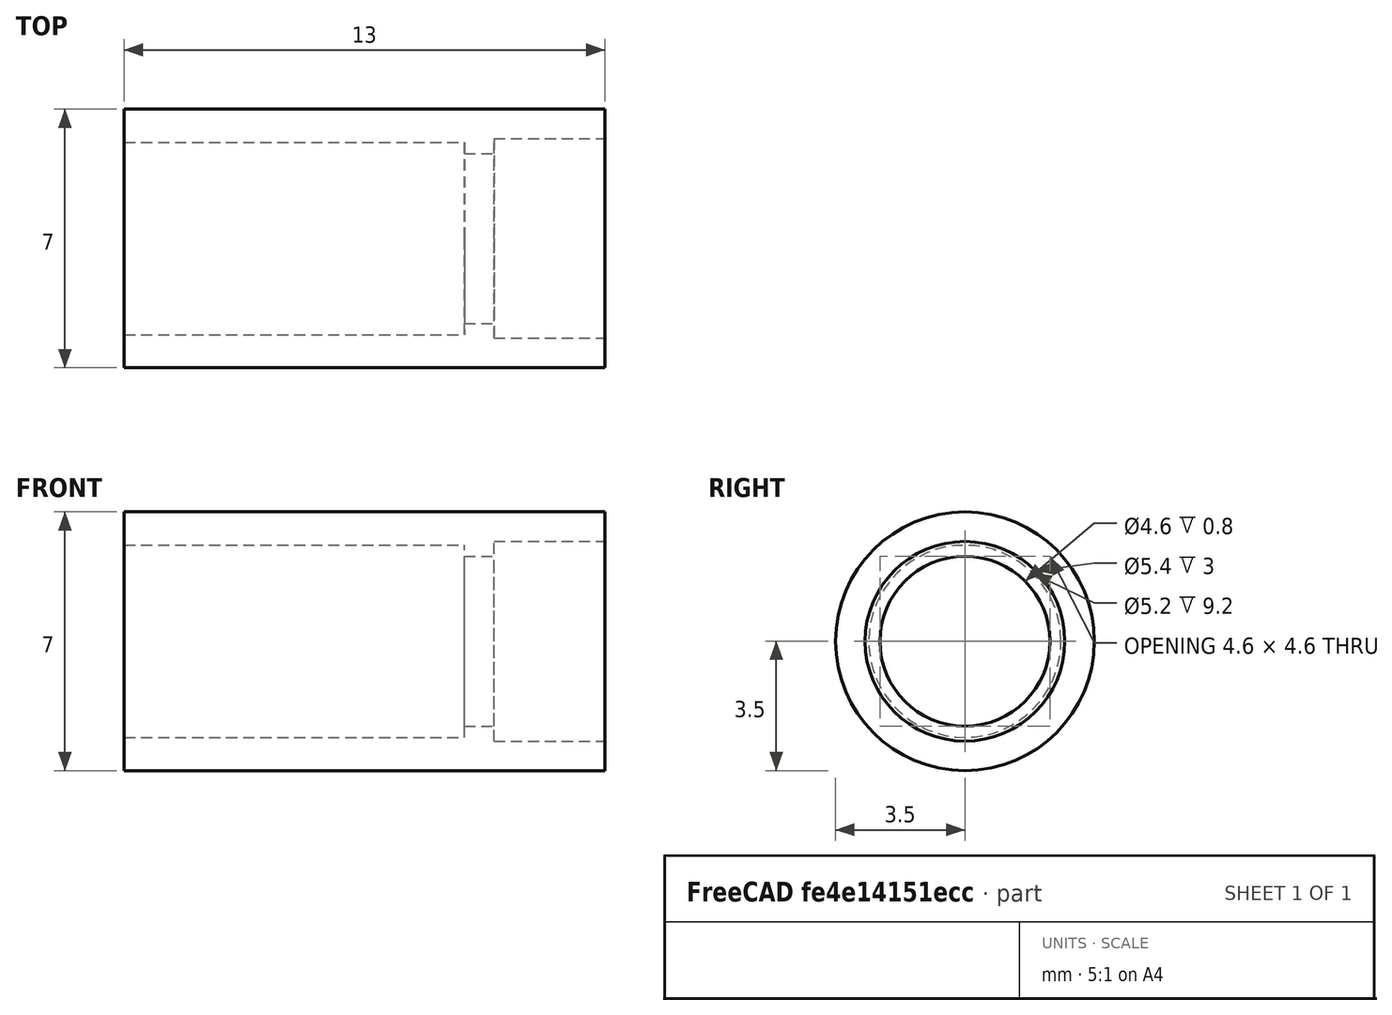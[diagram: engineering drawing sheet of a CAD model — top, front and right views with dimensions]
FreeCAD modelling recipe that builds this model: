
FCSTD DOCUMENT  (FreeCAD 0.14R3700 (Git))
Label: Vactrol_20150325
License: CC-BY 3.0
LicenseURL: http://creativecommons.org/licenses/by/3.0/
objects: Part::Cylinder×4, Part::Cut×3
note: 7 computed .brp shape members not serialized (recipe doc carries the construction recipe); baked Part::Feature solids carry a one-line shape summary decoded from their .brp

FEATURE [Part::Cylinder] Cylinder
  Angle = 360
  Height = 13
  Placement = pos=(0,0,0) rot=(0,1,0;1.5708rad)
  Radius = 3.5
FEATURE [Part::Cylinder] Cylinder001  label="light_channel"
  Angle = 360
  Height = 13
  Placement = pos=(0,0,0) rot=(0,1,0;1.5708rad)
  Radius = 2.3
FEATURE [Part::Cut] Cut  label="pipe"
  Base = -> Cylinder
  Tool = -> Cylinder001
FEATURE [Part::Cylinder] Cylinder002  label="LDR_hole"
  Angle = 360
  Height = 3
  Placement = pos=(10,0,0) rot=(0,1,0;1.5708rad)
  Radius = 2.7
FEATURE [Part::Cut] Cut001
  Base = -> Cut
  Tool = -> Cylinder002
FEATURE [Part::Cylinder] Cylinder003  label="LED_hole"
  Angle = 360
  Height = 9.2
  Placement = pos=(0,0,0) rot=(0,1,0;1.5708rad)
  Radius = 2.6
FEATURE [Part::Cut] Cut002
  Base = -> Cut001
  Tool = -> Cylinder003
